# Revit family: Window_System_Solutions-NanaWall-WA-68_Fixed_Window
name_source: partatom
category: Windows
revit_build: Autodesk Revit Architecture 2013 (Build: 20130531_2115(x64)
units: mm (PartAtom-declared; Revit-internal decimal feet)

## types (1)
- Fixed Window
    04 CSI = 08 52 00
    95 CSI = 8411
    Default Sill Height = 30"
    Description = Monumental Aluminum Framed Matching Windows and Doors
    Disclaimer = Please note that the Revit model is for schematic purposes only.  To obtain a detailed 3D model, please go to the NanaWall's configurator at www.nanawall.com.
    Exterior Wall Offset = 3"
    Filler = Rubber - NanaWall - Black
    Glass Material = Glass - NanaWall - Generic
    Glazing Options = http://www.nanawall.com
    Height = 54"
    Installation and Service URL = http://www.nanawall.com
    Manufacturer = NanaWall Systems, Inc.
    Manufacturer Fax = (415) 383-0312
    Model = WA 68 Fixed Window
    NanaWall Configurator = http://www.nanawall.com
    Product Documentation Link = http://www.nanawall.com
    Product Page URL = http://www.nanawall.com
    Rough Height = 52 39/64"
    Rough Width = 34 39/64"
    Sash = Metal - NanaWall - Aluminum
    Subcategory = Window
    URL = http://www.nanawall.com
    Wall Closure = By host
    Warranty URL = http://www.nanawall.com
    Width = 36"

## geometry (parser evidence)
native form markers: Blend x10, Sweep x4
no freeform markers — native parametric forms only
